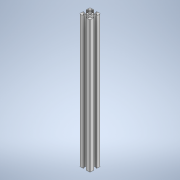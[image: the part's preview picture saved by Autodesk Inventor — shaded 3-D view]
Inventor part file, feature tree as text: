
AUTODESK INVENTOR PART (.ipt)
format: ipt  version: 2020 (Build 240168000, 168)  size: 164,864 bytes
history: native  units: mm
features: extrude x1, fillet x1, sketch x1
ambient origin geometry x8: Origin, YZ Plane, XZ Plane, XY Plane, X Axis, Y Axis, Z Axis, Center Point
bodies: Solide1 (feature_tree)
feature tree (3):
  extrude  "Extrusion1"  Depth=5.0mm
  fillet  "Congé1"  Radius=3.0mm
  sketch  "Esquisse1"
